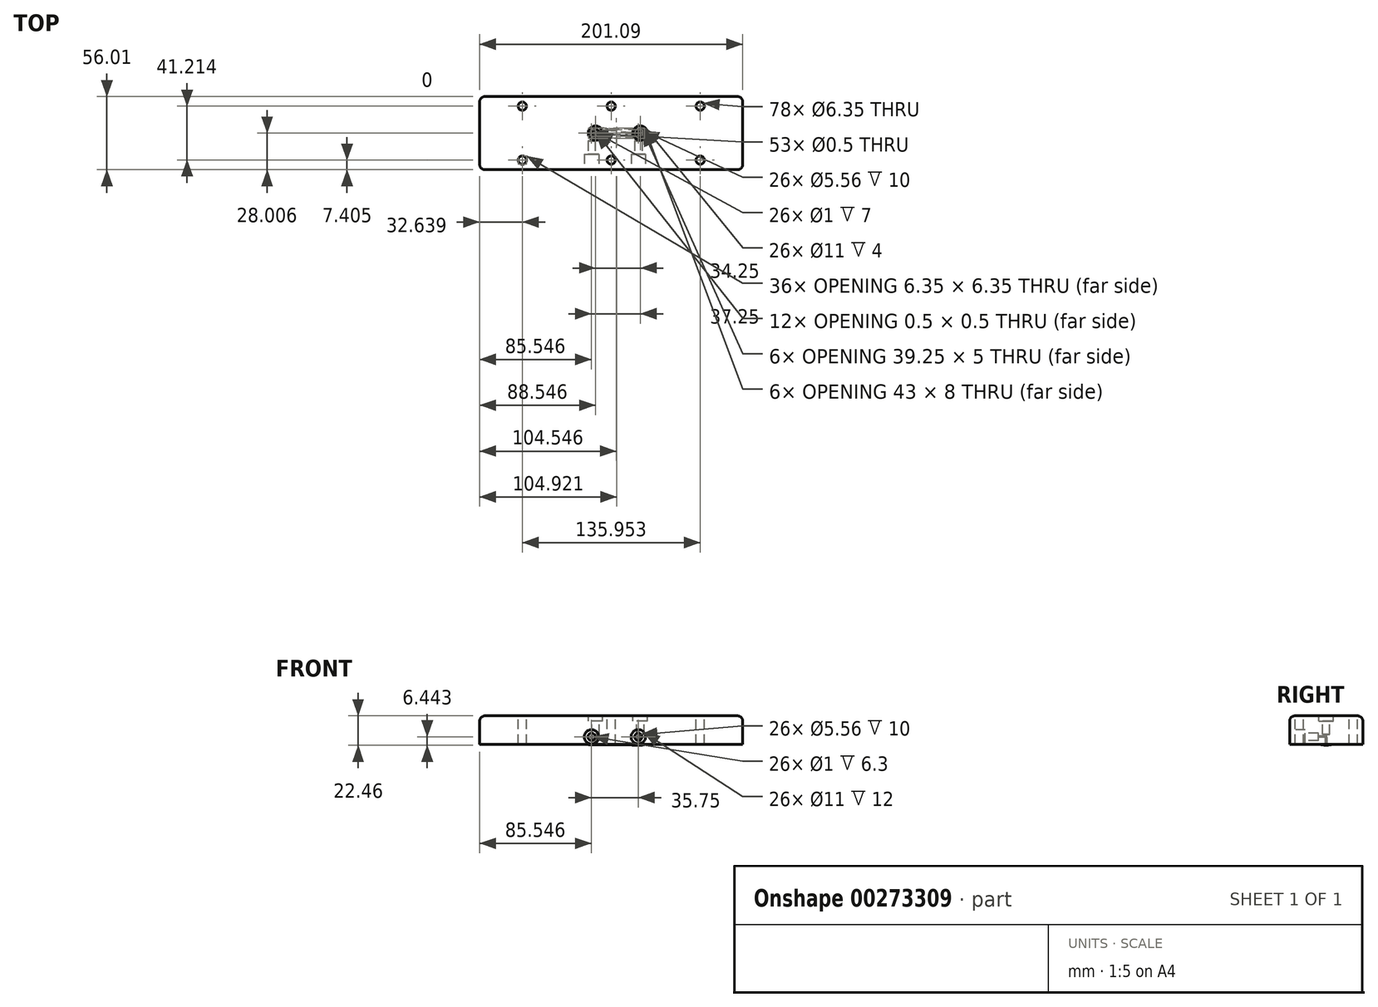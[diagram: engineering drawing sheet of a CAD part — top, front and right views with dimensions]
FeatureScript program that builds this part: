
annotation { "Feature Type Name" : "Feature", "Feature Type Description" : "" }
export const myFeature = defineFeature(function(context is Context, id is Id, definition is map)
    precondition{}
    {
        {
            var Q0;
            Q0=qCreatedBy(makeId("Top.planeOp"),FACE);
            var sketch = newSketch(context, id + "F0", { "sketchPlane" : qUnion([Q0])});
            skLineSegment(sketch, "E0.bottom", {"start": v(4.06, 0) * mm, "end": v(197.03, 0) * mm});
            skLineSegment(sketch, "E0.top", {"start": v(4.06, -56) * mm, "end": v(197.03, -56) * mm});
            skLineSegment(sketch, "E0.left", {"start": v(0, -4.06) * mm, "end": v(0, -51.94) * mm});
            skLineSegment(sketch, "E0.right", {"start": v(201.1, -4.06) * mm, "end": v(201.1, -51.94) * mm});
            skLineSegment(sketch, "E1.bottom", {"start": v(0, 0) * mm, "end": v(201.1, 0) * mm, "construction": true});
            skLineSegment(sketch, "E1.top", {"start": v(0, -7.4) * mm, "end": v(201.1, -7.4) * mm, "construction": true});
            skLineSegment(sketch, "E1.left", {"start": v(0, 0) * mm, "end": v(0, -7.4) * mm, "construction": true});
            skLineSegment(sketch, "E1.right", {"start": v(201.1, 0) * mm, "end": v(201.1, -7.4) * mm, "construction": true});
            skLineSegment(sketch, "E2.bottom", {"start": v(0, 0) * mm, "end": v(32.64, 0) * mm, "construction": true});
            skLineSegment(sketch, "E2.top", {"start": v(0, -56) * mm, "end": v(32.64, -56) * mm, "construction": true});
            skLineSegment(sketch, "E2.left", {"start": v(0, 0) * mm, "end": v(0, -56) * mm, "construction": true});
            skLineSegment(sketch, "E2.right", {"start": v(32.64, 0) * mm, "end": v(32.64, -56) * mm, "construction": true});
            skLineSegment(sketch, "E3.bottom", {"start": v(0, 0) * mm, "end": v(168.6, 0) * mm, "construction": true});
            skLineSegment(sketch, "E3.top", {"start": v(0, -56) * mm, "end": v(168.6, -56) * mm, "construction": true});
            skLineSegment(sketch, "E3.right", {"start": v(168.6, 0) * mm, "end": v(168.6, -56) * mm, "construction": true});
            skLineSegment(sketch, "E4.bottom", {"start": v(0, 0) * mm, "end": v(100.57, 0) * mm, "construction": true});
            skLineSegment(sketch, "E4.top", {"start": v(0, -56) * mm, "end": v(100.57, -56) * mm, "construction": true});
            skLineSegment(sketch, "E4.right", {"start": v(100.57, 0) * mm, "end": v(100.57, -56) * mm, "construction": true});
            skLineSegment(sketch, "E5.top", {"start": v(0, -48.6) * mm, "end": v(201.1, -48.6) * mm, "construction": true});
            skLineSegment(sketch, "E5.left", {"start": v(0, 0) * mm, "end": v(0, -48.6) * mm, "construction": true});
            skLineSegment(sketch, "E5.right", {"start": v(201.1, 0) * mm, "end": v(201.1, -48.6) * mm, "construction": true});
            skLineSegment(sketch, "E6.bottom", {"start": v(0, 0) * mm, "end": v(52.5, 0) * mm, "construction": true});
            skLineSegment(sketch, "E6.top", {"start": v(0, -56) * mm, "end": v(52.5, -56) * mm, "construction": true});
            skLineSegment(sketch, "E6.right", {"start": v(52.5, 0) * mm, "end": v(52.5, -56) * mm, "construction": true});
            skCircle(sketch, "E7", {"center": v(32.64, -7.4) * mm, "radius": 3.18 * mm});
            skCircle(sketch, "E8", {"center": v(100.57, -7.4) * mm, "radius": 3.18 * mm});
            skCircle(sketch, "E9", {"center": v(168.6, -7.4) * mm, "radius": 3.18 * mm});
            skCircle(sketch, "E10", {"center": v(168.6, -48.6) * mm, "radius": 3.18 * mm});
            skCircle(sketch, "E11", {"center": v(100.55, -48.6) * mm, "radius": 3.18 * mm});
            skCircle(sketch, "E12", {"center": v(32.64, -48.6) * mm, "radius": 3.18 * mm});
            skLineSegment(sketch, "E13.bottom", {"start": v(0, 0) * mm, "end": v(138.75, 0) * mm, "construction": true});
            skLineSegment(sketch, "E13.top", {"start": v(0, -56) * mm, "end": v(138.75, -56) * mm, "construction": true});
            skLineSegment(sketch, "E13.right", {"start": v(138.75, 0) * mm, "end": v(138.75, -56) * mm, "construction": true});
            skLineSegment(sketch, "E14.top", {"start": v(0, -56) * mm, "end": v(201.1, -56) * mm, "construction": true});
            skLineSegment(sketch, "E14.right", {"start": v(201.1, 0) * mm, "end": v(201.1, -56) * mm, "construction": true});
            skPoint(sketch, "E15.visualSharp", {"position": v(201.1, 0) * mm});
            skArc(sketch, "E15.filletArc", {"start": v(201.1, -4.06) * mm, "mid": v(199.9, -1.2) * mm, "end": v(197.03, 0) * mm});
            skPoint(sketch, "E16.visualSharp", {"position": v(0, -56) * mm});
            skArc(sketch, "E16.filletArc", {"start": v(0, -51.94) * mm, "mid": v(1.2, -54.82) * mm, "end": v(4.06, -56) * mm});
            skPoint(sketch, "E17.visualSharp", {"position": v(201.1, -56) * mm});
            skArc(sketch, "E17.filletArc", {"start": v(197.03, -56) * mm, "mid": v(199.9, -54.82) * mm, "end": v(201.1, -51.94) * mm});
            skPoint(sketch, "E18.visualSharp", {"position": v(0, 0) * mm});
            skArc(sketch, "E18.filletArc", {"start": v(4.06, 0) * mm, "mid": v(1.2, -1.2) * mm, "end": v(0, -4.06) * mm});
            skSolve(sketch);
        }
        {
            var Q0;
            Q0 = qSketchRegion(id + "F0", true);
            extrude(context, id + "F1", {"entities" : qUnion([Q0]), "oppositeDirection" : true, "depth" : 22.03 * mm});
        }
        {
            var Q0;
            Q0=makeQuery(id+"F1.opExtrude","CAP_FACE",FACE,{"disambiguationData":[OSD([sQuery(id+"F0.wireOp",EDGE,"E0.bottom"),sQuery(id+"F0.wireOp",EDGE,"E0.top"),sQuery(id+"F0.wireOp",EDGE,"E0.left"),sQuery(id+"F0.wireOp",EDGE,"E0.right"),sQuery(id+"F0.wireOp",EDGE,"E7"),sQuery(id+"F0.wireOp",EDGE,"E8"),sQuery(id+"F0.wireOp",EDGE,"E9"),sQuery(id+"F0.wireOp",EDGE,"E10"),sQuery(id+"F0.wireOp",EDGE,"E11"),sQuery(id+"F0.wireOp",EDGE,"E12"),sQuery(id+"F0.wireOp",EDGE,"E15.filletArc"),sQuery(id+"F0.wireOp",EDGE,"E16.filletArc"),sQuery(id+"F0.wireOp",EDGE,"E17.filletArc"),sQuery(id+"F0.wireOp",EDGE,"E18.filletArc")])],"isStart":false});
            var sketch = newSketch(context, id + "F2", { "sketchPlane" : qUnion([Q0])});
            skPoint(sketch, "E19.middle.positionSnap0", {"position": v(0, 28) * mm});
            skPoint(sketch, "E19.middle.positionSnap1", {"position": v(100.55, 56) * mm});
            skPoint(sketch, "E19.centerSnap0", {"position": v(0, 28) * mm});
            skPoint(sketch, "E19.centerSnap1", {"position": v(100.55, 56) * mm});
            skLineSegment(sketch, "E20.bottom", {"start": v(115.55, 25.5) * mm, "end": v(85.55, 25.5) * mm, "construction": true});
            skLineSegment(sketch, "E20.top", {"start": v(115.55, 30.5) * mm, "end": v(85.55, 30.5) * mm, "construction": true});
            skLineSegment(sketch, "E20.left", {"start": v(115.55, 25.5) * mm, "end": v(115.55, 30.5) * mm, "construction": true});
            skLineSegment(sketch, "E20.right", {"start": v(85.55, 25.5) * mm, "end": v(85.55, 30.5) * mm, "construction": true});
            skPoint(sketch, "E20.middle", {"position": v(100.55, 28) * mm});
            skLineSegment(sketch, "E21.bottom", {"start": v(85.55, 30.5) * mm, "end": v(88.55, 30.5) * mm, "construction": true});
            skLineSegment(sketch, "E21.top", {"start": v(85.55, 25.5) * mm, "end": v(88.55, 25.5) * mm, "construction": true});
            skLineSegment(sketch, "E21.left", {"start": v(85.55, 30.5) * mm, "end": v(85.55, 25.5) * mm, "construction": true});
            skLineSegment(sketch, "E21.right", {"start": v(88.55, 30.5) * mm, "end": v(88.55, 25.5) * mm, "construction": true});
            skLineSegment(sketch, "E22.bottom", {"start": v(121.6, 27.73) * mm, "end": v(109.5, 27.73) * mm, "construction": true});
            skLineSegment(sketch, "E22.top", {"start": v(121.6, 28.28) * mm, "end": v(109.5, 28.28) * mm, "construction": true});
            skLineSegment(sketch, "E22.left", {"start": v(121.6, 27.73) * mm, "end": v(121.6, 28.28) * mm, "construction": true});
            skLineSegment(sketch, "E22.right", {"start": v(109.5, 27.73) * mm, "end": v(109.5, 28.28) * mm, "construction": true});
            skPoint(sketch, "E22.middle", {"position": v(115.55, 28) * mm});
            skArc(sketch, "E23", {"start": v(85.4, 28.2) * mm, "mid": v(85.3, 28) * mm, "end": v(85.4, 27.8) * mm});
            skLineSegment(sketch, "E24", {"start": v(88.55, 30.5) * mm, "end": v(85.4, 28.2) * mm});
            skLineSegment(sketch, "E25", {"start": v(88.55, 25.5) * mm, "end": v(85.4, 27.8) * mm});
            skLineSegment(sketch, "E26", {"start": v(88.55, 30.5) * mm, "end": v(115.55, 28.28) * mm});
            skLineSegment(sketch, "E27", {"start": v(115.55, 28.28) * mm, "end": v(121.6, 28.28) * mm});
            skLineSegment(sketch, "E28", {"start": v(121.6, 27.73) * mm, "end": v(115.55, 27.73) * mm});
            skLineSegment(sketch, "E29", {"start": v(115.55, 27.73) * mm, "end": v(88.55, 25.5) * mm});
            skLineSegment(sketch, "E30", {"start": v(121.6, 28.28) * mm, "end": v(121.6, 27.73) * mm});
            skSolve(sketch);
        }
        {
            var Q0;
            Q0 = qSketchRegion(id + "F2", true);
            extrude(context, id + "F3", {"entities" : qUnion([Q0]), "operationType" : NewBodyOperationType.REMOVE, "oppositeDirection" : true, "depth" : 0.25 * mm});
        }
        {
            var Q0;
            Q0=makeQuery(id+"F3.boolean.opBoolean","COPY",FACE,{"derivedFrom":makeQuery(id+"F3.opExtrude","CAP_FACE",FACE,{"disambiguationData":[OSD([sQuery(id+"F2.wireOp",EDGE,"E23"),sQuery(id+"F2.wireOp",EDGE,"E24"),sQuery(id+"F2.wireOp",EDGE,"E25"),sQuery(id+"F2.wireOp",EDGE,"E26"),sQuery(id+"F2.wireOp",EDGE,"E27"),sQuery(id+"F2.wireOp",EDGE,"E28"),sQuery(id+"F2.wireOp",EDGE,"E29"),sQuery(id+"F2.wireOp",EDGE,"E30")])],"isStart":false})});
            var sketch = newSketch(context, id + "F4", { "sketchPlane" : qUnion([Q0])});
            skLineSegment(sketch, "E31.bottom", {"start": v(121.6, 28.28) * mm, "end": v(115.55, 28.28) * mm, "construction": true});
            skLineSegment(sketch, "E31.top", {"start": v(121.6, 27.73) * mm, "end": v(115.55, 27.73) * mm, "construction": true});
            skLineSegment(sketch, "E31.left", {"start": v(121.6, 28.28) * mm, "end": v(121.6, 27.73) * mm, "construction": true});
            skLineSegment(sketch, "E31.right", {"start": v(115.55, 28.28) * mm, "end": v(115.55, 27.73) * mm, "construction": true});
            skLineSegment(sketch, "E32.bottom", {"start": v(115.55, 28.28) * mm, "end": v(116.55, 28.28) * mm, "construction": true});
            skLineSegment(sketch, "E32.top", {"start": v(115.55, 27.73) * mm, "end": v(116.55, 27.73) * mm, "construction": true});
            skLineSegment(sketch, "E32.right", {"start": v(116.55, 28.28) * mm, "end": v(116.55, 27.73) * mm, "construction": true});
            skLineSegment(sketch, "E33.bottom", {"start": v(116.55, 28.28) * mm, "end": v(121.6, 28.28) * mm});
            skLineSegment(sketch, "E33.top", {"start": v(116.55, 27.73) * mm, "end": v(121.6, 27.73) * mm});
            skLineSegment(sketch, "E33.left", {"start": v(116.55, 28.28) * mm, "end": v(116.55, 27.73) * mm});
            skLineSegment(sketch, "E33.right", {"start": v(121.6, 28.28) * mm, "end": v(121.6, 27.73) * mm});
            skSolve(sketch);
        }
        {
            var Q0;
            Q0 = qSketchRegion(id + "F4", true);
            extrude(context, id + "F5", {"entities" : qUnion([Q0]), "operationType" : NewBodyOperationType.REMOVE, "oppositeDirection" : true, "depth" : 0.03 * mm});
        }
        {
            var Q0;
            Q0=makeQuery(id+"F1.opExtrude","CAP_FACE",FACE,{"disambiguationData":[OSD([sQuery(id+"F0.wireOp",EDGE,"E0.bottom"),sQuery(id+"F0.wireOp",EDGE,"E0.top"),sQuery(id+"F0.wireOp",EDGE,"E0.left"),sQuery(id+"F0.wireOp",EDGE,"E0.right"),sQuery(id+"F0.wireOp",EDGE,"E7"),sQuery(id+"F0.wireOp",EDGE,"E8"),sQuery(id+"F0.wireOp",EDGE,"E9"),sQuery(id+"F0.wireOp",EDGE,"E10"),sQuery(id+"F0.wireOp",EDGE,"E11"),sQuery(id+"F0.wireOp",EDGE,"E12"),sQuery(id+"F0.wireOp",EDGE,"E15.filletArc"),sQuery(id+"F0.wireOp",EDGE,"E16.filletArc"),sQuery(id+"F0.wireOp",EDGE,"E17.filletArc"),sQuery(id+"F0.wireOp",EDGE,"E18.filletArc")])],"isStart":false});
            var sketch = newSketch(context, id + "F6", { "sketchPlane" : qUnion([Q0])});
            skLineSegment(sketch, "E34.bottom", {"start": v(115.55, 30.5) * mm, "end": v(85.55, 30.5) * mm, "construction": true});
            skLineSegment(sketch, "E34.top", {"start": v(115.55, 25.5) * mm, "end": v(85.55, 25.5) * mm, "construction": true});
            skLineSegment(sketch, "E34.left", {"start": v(115.55, 30.5) * mm, "end": v(115.55, 25.5) * mm, "construction": true});
            skLineSegment(sketch, "E34.right", {"start": v(85.55, 30.5) * mm, "end": v(85.55, 25.5) * mm, "construction": true});
            skPoint(sketch, "E34.middle", {"position": v(100.55, 28) * mm});
            skPoint(sketch, "E34.middle.positionSnap0", {"position": v(0, 28) * mm});
            skPoint(sketch, "E34.middle.positionSnap1", {"position": v(100.55, 56) * mm});
            skPoint(sketch, "E34.centerSnap0", {"position": v(0, 28) * mm});
            skPoint(sketch, "E34.centerSnap1", {"position": v(100.55, 56) * mm});
            skLineSegment(sketch, "E35.bottom", {"start": v(85.55, 30.5) * mm, "end": v(88.55, 30.5) * mm, "construction": true});
            skLineSegment(sketch, "E35.top", {"start": v(85.55, 25.5) * mm, "end": v(88.55, 25.5) * mm, "construction": true});
            skLineSegment(sketch, "E35.right", {"start": v(88.55, 30.5) * mm, "end": v(88.55, 25.5) * mm, "construction": true});
            skCircle(sketch, "E36", {"center": v(88.55, 28) * mm, "radius": 0.25 * mm});
            skPoint(sketch, "E37.middle", {"position": v(115.55, 28) * mm});
            skLineSegment(sketch, "E38.bottom", {"start": v(122.8, 27.73) * mm, "end": v(108.3, 27.73) * mm, "construction": true});
            skLineSegment(sketch, "E38.top", {"start": v(122.8, 28.28) * mm, "end": v(108.3, 28.28) * mm, "construction": true});
            skLineSegment(sketch, "E38.left", {"start": v(122.8, 27.73) * mm, "end": v(122.8, 28.28) * mm, "construction": true});
            skLineSegment(sketch, "E38.right", {"start": v(108.3, 27.73) * mm, "end": v(108.3, 28.28) * mm, "construction": true});
            skPoint(sketch, "E38.cornerSnap0", {"position": v(118.57, 27.73) * mm});
            skCircle(sketch, "E39", {"center": v(122.8, 28) * mm, "radius": 0.25 * mm});
            skSolve(sketch);
        }
        {
            var Q0;
            Q0 = qSketchRegion(id + "F6", true);
            extrude(context, id + "F7", {"entities" : qUnion([Q0]), "operationType" : NewBodyOperationType.REMOVE, "endBound" : BoundingType.THROUGH_ALL, "oppositeDirection" : true, "depth" : 11 * mm});
        }
        {
            var Q0;
            Q0=makeQuery(id+"F1.opExtrude","CAP_FACE",FACE,{"disambiguationData":[OSD([sQuery(id+"F0.wireOp",EDGE,"E0.bottom"),sQuery(id+"F0.wireOp",EDGE,"E0.top"),sQuery(id+"F0.wireOp",EDGE,"E0.left"),sQuery(id+"F0.wireOp",EDGE,"E0.right"),sQuery(id+"F0.wireOp",EDGE,"E7"),sQuery(id+"F0.wireOp",EDGE,"E8"),sQuery(id+"F0.wireOp",EDGE,"E9"),sQuery(id+"F0.wireOp",EDGE,"E10"),sQuery(id+"F0.wireOp",EDGE,"E11"),sQuery(id+"F0.wireOp",EDGE,"E12"),sQuery(id+"F0.wireOp",EDGE,"E15.filletArc"),sQuery(id+"F0.wireOp",EDGE,"E16.filletArc"),sQuery(id+"F0.wireOp",EDGE,"E17.filletArc"),sQuery(id+"F0.wireOp",EDGE,"E18.filletArc")])],"isStart":true});
            var sketch = newSketch(context, id + "F8", { "sketchPlane" : qUnion([Q0])});
            skCircle(sketch, "E40", {"center": v(122.8, -28) * mm, "radius": 0.5 * mm});
            skCircle(sketch, "E41", {"center": v(88.55, -28) * mm, "radius": 0.5 * mm});
            skSolve(sketch);
        }
        {
            var Q0;
            Q0=makeQuery(id+"F1.opExtrude","CAP_FACE",FACE,{"disambiguationData":[OSD([sQuery(id+"F0.wireOp",EDGE,"E0.bottom"),sQuery(id+"F0.wireOp",EDGE,"E0.top"),sQuery(id+"F0.wireOp",EDGE,"E0.left"),sQuery(id+"F0.wireOp",EDGE,"E0.right"),sQuery(id+"F0.wireOp",EDGE,"E7"),sQuery(id+"F0.wireOp",EDGE,"E8"),sQuery(id+"F0.wireOp",EDGE,"E9"),sQuery(id+"F0.wireOp",EDGE,"E10"),sQuery(id+"F0.wireOp",EDGE,"E11"),sQuery(id+"F0.wireOp",EDGE,"E12"),sQuery(id+"F0.wireOp",EDGE,"E15.filletArc"),sQuery(id+"F0.wireOp",EDGE,"E16.filletArc"),sQuery(id+"F0.wireOp",EDGE,"E17.filletArc"),sQuery(id+"F0.wireOp",EDGE,"E18.filletArc")])],"isStart":false});
            var sketch = newSketch(context, id + "F9", { "sketchPlane" : qUnion([Q0])});
            skLineSegment(sketch, "E42.bottom", {"start": v(115.55, 25.5) * mm, "end": v(85.55, 25.5) * mm, "construction": true});
            skLineSegment(sketch, "E42.top", {"start": v(115.55, 30.5) * mm, "end": v(85.55, 30.5) * mm, "construction": true});
            skLineSegment(sketch, "E42.left", {"start": v(115.55, 25.5) * mm, "end": v(115.55, 30.5) * mm, "construction": true});
            skLineSegment(sketch, "E42.right", {"start": v(85.55, 25.5) * mm, "end": v(85.55, 30.5) * mm, "construction": true});
            skPoint(sketch, "E42.middle", {"position": v(100.55, 28) * mm});
            skPoint(sketch, "E42.middle.positionSnap0", {"position": v(100.55, 56) * mm});
            skPoint(sketch, "E42.middle.positionSnap1", {"position": v(0, 28) * mm});
            skPoint(sketch, "E42.centerSnap0", {"position": v(100.55, 56) * mm});
            skPoint(sketch, "E42.centerSnap1", {"position": v(0, 28) * mm});
            skLineSegment(sketch, "E43.bottom", {"start": v(85.55, 30.5) * mm, "end": v(88.55, 30.5) * mm, "construction": true});
            skLineSegment(sketch, "E43.top", {"start": v(85.55, 25.5) * mm, "end": v(88.55, 25.5) * mm, "construction": true});
            skLineSegment(sketch, "E43.left", {"start": v(85.55, 30.5) * mm, "end": v(85.55, 25.5) * mm, "construction": true});
            skLineSegment(sketch, "E43.right", {"start": v(88.55, 30.5) * mm, "end": v(88.55, 25.5) * mm, "construction": true});
            skCircle(sketch, "E44", {"center": v(85.55, 28) * mm, "radius": 0.25 * mm});
            skLineSegment(sketch, "E45.bottom", {"start": v(121.3, 27.75) * mm, "end": v(109.8, 27.75) * mm, "construction": true});
            skLineSegment(sketch, "E45.top", {"start": v(121.3, 28.25) * mm, "end": v(109.8, 28.25) * mm, "construction": true});
            skLineSegment(sketch, "E45.left", {"start": v(121.3, 27.75) * mm, "end": v(121.3, 28.25) * mm, "construction": true});
            skLineSegment(sketch, "E45.right", {"start": v(109.8, 27.75) * mm, "end": v(109.8, 28.25) * mm, "construction": true});
            skPoint(sketch, "E45.middle", {"position": v(115.55, 28) * mm});
            skCircle(sketch, "E46", {"center": v(121.3, 28) * mm, "radius": 0.25 * mm});
            skSolve(sketch);
        }
        {
            var Q0;
            Q0 = qSketchRegion(id + "F9", true);
            extrude(context, id + "F10", {"entities" : qUnion([Q0]), "operationType" : NewBodyOperationType.REMOVE, "oppositeDirection" : true, "depth" : 6 * mm});
        }
        {
            var Q0;
            Q0=makeQuery(id+"F1.opExtrude","SWEPT_FACE",FACE,{"disambiguationData":[OSD([sQuery(id+"F0.wireOp",EDGE,"E0.top")])]});
            var sketch = newSketch(context, id + "F11", { "sketchPlane" : qUnion([Q0])});
            skLineSegment(sketch, "E47.bottom", {"start": v(115.55, -16.02) * mm, "end": v(85.55, -16.02) * mm, "construction": true});
            skLineSegment(sketch, "E47.top", {"start": v(115.55, -6.02) * mm, "end": v(85.55, -6.02) * mm, "construction": true});
            skLineSegment(sketch, "E47.left", {"start": v(115.55, -16.02) * mm, "end": v(115.55, -6.02) * mm, "construction": true});
            skLineSegment(sketch, "E47.right", {"start": v(85.55, -16.02) * mm, "end": v(85.55, -6.02) * mm, "construction": true});
            skPoint(sketch, "E47.middle", {"position": v(100.55, -11.02) * mm});
            skPoint(sketch, "E47.middle.positionSnap0", {"position": v(4.06, -11.02) * mm});
            skPoint(sketch, "E47.middle.positionSnap1", {"position": v(100.55, -22.03) * mm});
            skPoint(sketch, "E47.centerSnap0", {"position": v(4.06, -11.02) * mm});
            skPoint(sketch, "E47.centerSnap1", {"position": v(100.55, -22.03) * mm});
            skPoint(sketch, "E48.middle", {"position": v(115.55, -11.02) * mm});
            skLineSegment(sketch, "E49.bottom", {"start": v(115.55, -13.52) * mm, "end": v(85.55, -13.52) * mm, "construction": true});
            skLineSegment(sketch, "E49.top", {"start": v(115.55, -8.52) * mm, "end": v(85.55, -8.52) * mm, "construction": true});
            skLineSegment(sketch, "E49.left", {"start": v(115.55, -13.52) * mm, "end": v(115.55, -8.52) * mm, "construction": true});
            skLineSegment(sketch, "E49.right", {"start": v(85.55, -13.52) * mm, "end": v(85.55, -8.52) * mm, "construction": true});
            skLineSegment(sketch, "E50.bottom", {"start": v(121.3, -12.02) * mm, "end": v(109.8, -12.02) * mm, "construction": true});
            skLineSegment(sketch, "E50.top", {"start": v(121.3, -10.02) * mm, "end": v(109.8, -10.02) * mm, "construction": true});
            skLineSegment(sketch, "E50.left", {"start": v(121.3, -12.02) * mm, "end": v(121.3, -10.02) * mm, "construction": true});
            skLineSegment(sketch, "E50.right", {"start": v(109.8, -12.02) * mm, "end": v(109.8, -10.02) * mm, "construction": true});
            skCircle(sketch, "E51", {"center": v(121.3, -16.02) * mm, "radius": 0.5 * mm});
            skCircle(sketch, "E52", {"center": v(85.55, -16.02) * mm, "radius": 0.5 * mm});
            skLineSegment(sketch, "E53", {"start": v(100.55, -16.02) * mm, "end": v(121.3, -16.02) * mm, "construction": true});
            skLineSegment(sketch, "E54.bottom", {"start": v(85.55, -13.52) * mm, "end": v(85.55, -13.52) * mm});
            skLineSegment(sketch, "E54.right", {"start": v(85.55, -13.52) * mm, "end": v(85.55, -16.02) * mm, "construction": true});
            skSolve(sketch);
        }
        {
            var Q0;
            Q0 = qSketchRegion(id + "F11", true);
            extrude(context, id + "F12", {"entities" : qUnion([Q0]), "operationType" : NewBodyOperationType.REMOVE, "oppositeDirection" : true, "depth" : 28.3 * mm});
        }
        {
            var Q0;
            Q0=makeQuery(id+"F1.opExtrude","CAP_FACE",FACE,{"disambiguationData":[OSD([sQuery(id+"F0.wireOp",EDGE,"E0.bottom"),sQuery(id+"F0.wireOp",EDGE,"E0.top"),sQuery(id+"F0.wireOp",EDGE,"E0.left"),sQuery(id+"F0.wireOp",EDGE,"E0.right"),sQuery(id+"F0.wireOp",EDGE,"E7"),sQuery(id+"F0.wireOp",EDGE,"E8"),sQuery(id+"F0.wireOp",EDGE,"E9"),sQuery(id+"F0.wireOp",EDGE,"E10"),sQuery(id+"F0.wireOp",EDGE,"E11"),sQuery(id+"F0.wireOp",EDGE,"E12"),sQuery(id+"F0.wireOp",EDGE,"E15.filletArc"),sQuery(id+"F0.wireOp",EDGE,"E16.filletArc"),sQuery(id+"F0.wireOp",EDGE,"E17.filletArc"),sQuery(id+"F0.wireOp",EDGE,"E18.filletArc")])],"isStart":true});
            var sketch = newSketch(context, id + "F13", { "sketchPlane" : qUnion([Q0])});
            skCircle(sketch, "E55", {"center": v(88.55, -28) * mm, "radius": 2.78 * mm});
            skCircle(sketch, "E56", {"center": v(122.8, -28) * mm, "radius": 2.78 * mm});
            skSolve(sketch);
        }
        {
            var Q0;
            Q0 = qSketchRegion(id + "F13", true);
            extrude(context, id + "F14", {"entities" : qUnion([Q0]), "operationType" : NewBodyOperationType.REMOVE, "oppositeDirection" : true, "depth" : 14 * mm});
        }
        {
            var Q0;
            Q0 = qSketchRegion(id + "F8", true);
            extrude(context, id + "F15", {"entities" : qUnion([Q0]), "operationType" : NewBodyOperationType.REMOVE, "oppositeDirection" : true, "depth" : 21 * mm});
        }
        {
            var Q0;
            Q0=makeQuery(id+"F1.opExtrude","SWEPT_FACE",FACE,{"disambiguationData":[OSD([sQuery(id+"F0.wireOp",EDGE,"E0.top")])]});
            var sketch = newSketch(context, id + "F16", { "sketchPlane" : qUnion([Q0])});
            skCircle(sketch, "E57", {"center": v(121.3, -16.02) * mm, "radius": 2.78 * mm});
            skCircle(sketch, "E58", {"center": v(85.55, -16.02) * mm, "radius": 2.78 * mm});
            skSolve(sketch);
        }
        {
            var Q0;
            Q0 = qSketchRegion(id + "F16", true);
            extrude(context, id + "F17", {"entities" : qUnion([Q0]), "operationType" : NewBodyOperationType.REMOVE, "oppositeDirection" : true, "depth" : 22 * mm});
        }
        {
            var Q0;
            Q0=makeQuery(id+"F1.opExtrude","CAP_FACE",FACE,{"disambiguationData":[OSD([sQuery(id+"F0.wireOp",EDGE,"E0.bottom"),sQuery(id+"F0.wireOp",EDGE,"E0.top"),sQuery(id+"F0.wireOp",EDGE,"E0.left"),sQuery(id+"F0.wireOp",EDGE,"E0.right"),sQuery(id+"F0.wireOp",EDGE,"E7"),sQuery(id+"F0.wireOp",EDGE,"E8"),sQuery(id+"F0.wireOp",EDGE,"E9"),sQuery(id+"F0.wireOp",EDGE,"E10"),sQuery(id+"F0.wireOp",EDGE,"E11"),sQuery(id+"F0.wireOp",EDGE,"E12"),sQuery(id+"F0.wireOp",EDGE,"E15.filletArc"),sQuery(id+"F0.wireOp",EDGE,"E16.filletArc"),sQuery(id+"F0.wireOp",EDGE,"E17.filletArc"),sQuery(id+"F0.wireOp",EDGE,"E18.filletArc")])],"isStart":false});
            var sketch = newSketch(context, id + "F18", { "sketchPlane" : qUnion([Q0])});
            skLineSegment(sketch, "E59.bottom", {"start": v(115.55, 28.28) * mm, "end": v(116.55, 28.28) * mm, "construction": true});
            skLineSegment(sketch, "E59.top", {"start": v(115.55, 27.73) * mm, "end": v(116.55, 27.73) * mm, "construction": true});
            skLineSegment(sketch, "E59.left", {"start": v(115.55, 28.28) * mm, "end": v(115.55, 27.73) * mm, "construction": true});
            skLineSegment(sketch, "E59.right", {"start": v(116.55, 28.28) * mm, "end": v(116.55, 27.73) * mm, "construction": true});
            skLineSegment(sketch, "E60.bottom", {"start": v(124.55, 26.25) * mm, "end": v(108.55, 26.25) * mm, "construction": true});
            skLineSegment(sketch, "E60.top", {"start": v(124.55, 29.75) * mm, "end": v(108.55, 29.75) * mm, "construction": true});
            skLineSegment(sketch, "E60.left", {"start": v(124.55, 26.25) * mm, "end": v(124.55, 29.75) * mm, "construction": true});
            skLineSegment(sketch, "E60.right", {"start": v(108.55, 26.25) * mm, "end": v(108.55, 29.75) * mm, "construction": true});
            skPoint(sketch, "E60.middle", {"position": v(116.55, 28) * mm});
            skLineSegment(sketch, "E61.bottom", {"start": v(124.55, 29.75) * mm, "end": v(116.55, 29.75) * mm});
            skLineSegment(sketch, "E61.top", {"start": v(124.55, 26.25) * mm, "end": v(116.55, 26.25) * mm});
            skLineSegment(sketch, "E61.left", {"start": v(124.55, 29.75) * mm, "end": v(124.55, 26.25) * mm});
            skLineSegment(sketch, "E61.right", {"start": v(116.55, 29.75) * mm, "end": v(116.55, 26.25) * mm});
            skSolve(sketch);
        }
        {
            var Q0;
            Q0 = qSketchRegion(id + "F18", true);
            extrude(context, id + "F19", {"entities" : qUnion([Q0]), "operationType" : NewBodyOperationType.REMOVE, "oppositeDirection" : true, "depth" : 0.1 * mm});
        }
        {
            var Q0;
            Q0=makeQuery(id+"F1.opExtrude","CAP_FACE",FACE,{"disambiguationData":[OSD([sQuery(id+"F0.wireOp",EDGE,"E0.bottom"),sQuery(id+"F0.wireOp",EDGE,"E0.top"),sQuery(id+"F0.wireOp",EDGE,"E0.left"),sQuery(id+"F0.wireOp",EDGE,"E0.right"),sQuery(id+"F0.wireOp",EDGE,"E7"),sQuery(id+"F0.wireOp",EDGE,"E8"),sQuery(id+"F0.wireOp",EDGE,"E9"),sQuery(id+"F0.wireOp",EDGE,"E10"),sQuery(id+"F0.wireOp",EDGE,"E11"),sQuery(id+"F0.wireOp",EDGE,"E12"),sQuery(id+"F0.wireOp",EDGE,"E15.filletArc"),sQuery(id+"F0.wireOp",EDGE,"E16.filletArc"),sQuery(id+"F0.wireOp",EDGE,"E17.filletArc"),sQuery(id+"F0.wireOp",EDGE,"E18.filletArc")])],"isStart":false});
            var sketch = newSketch(context, id + "F20", { "sketchPlane" : qUnion([Q0])});
            skLineSegment(sketch, "E62.bottom", {"start": v(118.05, 24) * mm, "end": v(83.05, 24) * mm, "construction": true});
            skLineSegment(sketch, "E62.top", {"start": v(118.05, 32) * mm, "end": v(83.05, 32) * mm, "construction": true});
            skLineSegment(sketch, "E62.left", {"start": v(118.05, 24) * mm, "end": v(118.05, 32) * mm, "construction": true});
            skLineSegment(sketch, "E62.right", {"start": v(83.05, 24) * mm, "end": v(83.05, 32) * mm, "construction": true});
            skPoint(sketch, "E62.middle", {"position": v(100.55, 28) * mm});
            skPoint(sketch, "E62.middle.positionSnap0", {"position": v(0, 28) * mm});
            skPoint(sketch, "E62.middle.positionSnap1", {"position": v(100.55, 56) * mm});
            skPoint(sketch, "E62.centerSnap0", {"position": v(0, 28) * mm});
            skPoint(sketch, "E62.centerSnap1", {"position": v(100.55, 56) * mm});
            skLineSegment(sketch, "E63.bottom", {"start": v(83.05, 32) * mm, "end": v(88.55, 32) * mm, "construction": true});
            skLineSegment(sketch, "E63.top", {"start": v(83.05, 24) * mm, "end": v(88.55, 24) * mm, "construction": true});
            skLineSegment(sketch, "E63.left", {"start": v(83.05, 32) * mm, "end": v(83.05, 24) * mm, "construction": true});
            skLineSegment(sketch, "E63.right", {"start": v(88.55, 32) * mm, "end": v(88.55, 24) * mm, "construction": true});
            skLineSegment(sketch, "E64.bottom", {"start": v(126.05, 31) * mm, "end": v(110.05, 31) * mm, "construction": true});
            skLineSegment(sketch, "E64.top", {"start": v(126.05, 25) * mm, "end": v(110.05, 25) * mm, "construction": true});
            skLineSegment(sketch, "E64.left", {"start": v(126.05, 31) * mm, "end": v(126.05, 25) * mm, "construction": true});
            skLineSegment(sketch, "E64.right", {"start": v(110.05, 31) * mm, "end": v(110.05, 25) * mm, "construction": true});
            skPoint(sketch, "E64.middle", {"position": v(118.05, 28) * mm});
            skLineSegment(sketch, "E65", {"start": v(88.55, 32) * mm, "end": v(118.05, 31) * mm});
            skLineSegment(sketch, "E66", {"start": v(118.05, 31) * mm, "end": v(126.05, 31) * mm});
            skLineSegment(sketch, "E67", {"start": v(126.05, 25) * mm, "end": v(118.05, 25) * mm});
            skLineSegment(sketch, "E68", {"start": v(118.05, 25) * mm, "end": v(88.55, 24) * mm});
            skLineSegment(sketch, "E69", {"start": v(88.55, 24) * mm, "end": v(83.05, 28) * mm});
            skPoint(sketch, "E69.endSnap0", {"position": v(83.05, 28) * mm});
            skLineSegment(sketch, "E70", {"start": v(83.05, 28) * mm, "end": v(88.55, 32) * mm});
            skLineSegment(sketch, "E71", {"start": v(126.05, 31) * mm, "end": v(126.05, 25) * mm});
            skLineSegment(sketch, "E72.bottom", {"start": v(201.1, 56) * mm, "end": v(0, 56) * mm});
            skLineSegment(sketch, "E72.top", {"start": v(201.1, 0) * mm, "end": v(0, 0) * mm});
            skLineSegment(sketch, "E72.left", {"start": v(201.1, 56) * mm, "end": v(201.1, 0) * mm});
            skLineSegment(sketch, "E72.right", {"start": v(0, 56) * mm, "end": v(0, 0) * mm});
            skSolve(sketch);
        }
        {
            var Q0;
            Q0 = qSketchRegion(id + "F20", true);
            extrude(context, id + "F21", {"entities" : qUnion([Q0]), "operationType" : NewBodyOperationType.REMOVE, "oppositeDirection" : true, "depth" : .4 * mm});
        }
        {
            var Q0;
            Q0=makeQuery(id+"F19.boolean.opBoolean","COPY",FACE,{"derivedFrom":makeQuery(id+"F19.opExtrude","CAP_FACE",FACE,{"disambiguationData":[OSD([sQuery(id+"F18.wireOp",EDGE,"E61.bottom"),sQuery(id+"F18.wireOp",EDGE,"E61.top"),sQuery(id+"F18.wireOp",EDGE,"E61.left"),sQuery(id+"F18.wireOp",EDGE,"E61.right")])],"isStart":false})});
            var sketch = newSketch(context, id + "F22", { "sketchPlane" : qUnion([Q0])});
            skLineSegment(sketch, "E73.0", {"start": v(124.55, 29.75) * mm, "end": v(116.55, 29.75) * mm});
            skLineSegment(sketch, "E73.1", {"start": v(124.55, 29.75) * mm, "end": v(124.55, 26.25) * mm});
            skLineSegment(sketch, "E73.2", {"start": v(124.55, 26.25) * mm, "end": v(116.55, 26.25) * mm});
            skCircle(sketch, "E74.0", {"center": v(122.8, 28) * mm, "radius": 0.25 * mm});
            skLineSegment(sketch, "E75", {"start": v(116.55, 29.75) * mm, "end": v(116.55, 26.25) * mm});
            skSolve(sketch);
        }
        {
            var Q0;
            Q0 = qSketchRegion(id + "F22", true);
            extrude(context, id + "F23", {"entities" : qUnion([Q0]), "depth" : 0.03 * mm});
        }
        {
            var Q0;
            Q0=makeQuery(id+"F23.opExtrude","CAP_FACE",FACE,{"disambiguationData":[OSD([sQuery(id+"F22.wireOp",EDGE,"E73.0"),sQuery(id+"F22.wireOp",EDGE,"E73.1"),sQuery(id+"F22.wireOp",EDGE,"E73.2"),sQuery(id+"F22.wireOp",EDGE,"E74.0"),sQuery(id+"F22.wireOp",EDGE,"E75")])],"isStart":false});
            var sketch = newSketch(context, id + "F24", { "sketchPlane" : qUnion([Q0])});
            skLineSegment(sketch, "E76.0", {"start": v(124.55, 29.75) * mm, "end": v(116.55, 29.75) * mm});
            skLineSegment(sketch, "E77.0", {"start": v(124.55, 29.75) * mm, "end": v(124.55, 26.25) * mm});
            skLineSegment(sketch, "E78.0", {"start": v(124.55, 26.25) * mm, "end": v(116.55, 26.25) * mm});
            skLineSegment(sketch, "E79.0", {"start": v(116.55, 29.75) * mm, "end": v(116.55, 28.28) * mm});
            skLineSegment(sketch, "E80.0", {"start": v(116.55, 27.73) * mm, "end": v(116.55, 26.25) * mm});
            skLineSegment(sketch, "E81.bottom", {"start": v(116.55, 28.28) * mm, "end": v(123.1, 28.28) * mm});
            skLineSegment(sketch, "E81.top", {"start": v(116.55, 27.73) * mm, "end": v(123.1, 27.73) * mm});
            skLineSegment(sketch, "E81.right", {"start": v(123.1, 28.28) * mm, "end": v(123.1, 27.73) * mm});
            skSolve(sketch);
        }
        {
            var Q0;
            Q0 = qSketchRegion(id + "F24", true);
            extrude(context, id + "F25", {"entities" : qUnion([Q0]), "depth" : .5 * mm});
        }
        {
            var Q0;
            Q0=makeQuery(id+"F1.opExtrude","SWEPT_FACE",FACE,{"disambiguationData":[OSD([sQuery(id+"F0.wireOp",EDGE,"E0.top")])]});
            var sketch = newSketch(context, id + "F26", { "sketchPlane" : qUnion([Q0])});
            skCircle(sketch, "E82", {"center": v(85.55, -16.02) * mm, "radius": 5.5 * mm});
            skCircle(sketch, "E83", {"center": v(121.3, -16.02) * mm, "radius": 5.5 * mm});
            skSolve(sketch);
        }
        {
            var Q0;
            Q0 = qSketchRegion(id + "F26", true);
            extrude(context, id + "F27", {"entities" : qUnion([Q0]), "operationType" : NewBodyOperationType.REMOVE, "oppositeDirection" : true, "depth" : 12 * mm});
        }
        {
            var Q0;
            Q0=makeQuery(id+"F1.opExtrude","CAP_FACE",FACE,{"disambiguationData":[OSD([sQuery(id+"F0.wireOp",EDGE,"E0.bottom"),sQuery(id+"F0.wireOp",EDGE,"E0.top"),sQuery(id+"F0.wireOp",EDGE,"E0.left"),sQuery(id+"F0.wireOp",EDGE,"E0.right"),sQuery(id+"F0.wireOp",EDGE,"E7"),sQuery(id+"F0.wireOp",EDGE,"E8"),sQuery(id+"F0.wireOp",EDGE,"E9"),sQuery(id+"F0.wireOp",EDGE,"E10"),sQuery(id+"F0.wireOp",EDGE,"E11"),sQuery(id+"F0.wireOp",EDGE,"E12"),sQuery(id+"F0.wireOp",EDGE,"E15.filletArc"),sQuery(id+"F0.wireOp",EDGE,"E16.filletArc"),sQuery(id+"F0.wireOp",EDGE,"E17.filletArc"),sQuery(id+"F0.wireOp",EDGE,"E18.filletArc")])],"isStart":true});
            var sketch = newSketch(context, id + "F28", { "sketchPlane" : qUnion([Q0])});
            skCircle(sketch, "E84", {"center": v(88.55, -28) * mm, "radius": 5.5 * mm});
            skCircle(sketch, "E85", {"center": v(122.8, -28) * mm, "radius": 5.5 * mm});
            skSolve(sketch);
        }
        {
            var Q0;
            Q0 = qSketchRegion(id + "F28", true);
            extrude(context, id + "F29", {"entities" : qUnion([Q0]), "operationType" : NewBodyOperationType.REMOVE, "oppositeDirection" : true, "depth" : 4 * mm});
        }
        {
            var Q0;
            Q0=makeQuery(id+"F1.opExtrude","CAP_EDGE",EDGE,{"disambiguationData":[OSD([sQuery(id+"F0.wireOp",EDGE,"E0.top")])],"isStart":true});
            var Q1;
            Q1=makeQuery(id+"F1.opExtrude","CAP_EDGE",EDGE,{"disambiguationData":[OSD([sQuery(id+"F0.wireOp",EDGE,"E17.filletArc")])],"isStart":true});
            var Q2;
            Q2=makeQuery(id+"F1.opExtrude","CAP_EDGE",EDGE,{"disambiguationData":[OSD([sQuery(id+"F0.wireOp",EDGE,"E0.right")])],"isStart":true});
            var Q3;
            Q3=makeQuery(id+"F1.opExtrude","CAP_EDGE",EDGE,{"disambiguationData":[OSD([sQuery(id+"F0.wireOp",EDGE,"E15.filletArc")])],"isStart":true});
            var Q4;
            Q4=makeQuery(id+"F1.opExtrude","CAP_EDGE",EDGE,{"disambiguationData":[OSD([sQuery(id+"F0.wireOp",EDGE,"E0.bottom")])],"isStart":true});
            var Q5;
            Q5=makeQuery(id+"F1.opExtrude","CAP_EDGE",EDGE,{"disambiguationData":[OSD([sQuery(id+"F0.wireOp",EDGE,"E18.filletArc")])],"isStart":true});
            var Q6;
            Q6=makeQuery(id+"F1.opExtrude","CAP_EDGE",EDGE,{"disambiguationData":[OSD([sQuery(id+"F0.wireOp",EDGE,"E0.left")])],"isStart":true});
            var Q7;
            Q7=makeQuery(id+"F1.opExtrude","CAP_EDGE",EDGE,{"disambiguationData":[OSD([sQuery(id+"F0.wireOp",EDGE,"E16.filletArc")])],"isStart":true});
            fillet(context, id + "F30", {"entities" : qUnion([Q0, Q1, Q2, Q3, Q4, Q5, Q6, Q7]), "radius" : 4.06 * mm, "tangentPropagation" : true, "allowEdgeOverflow" : false});
        }
    });
